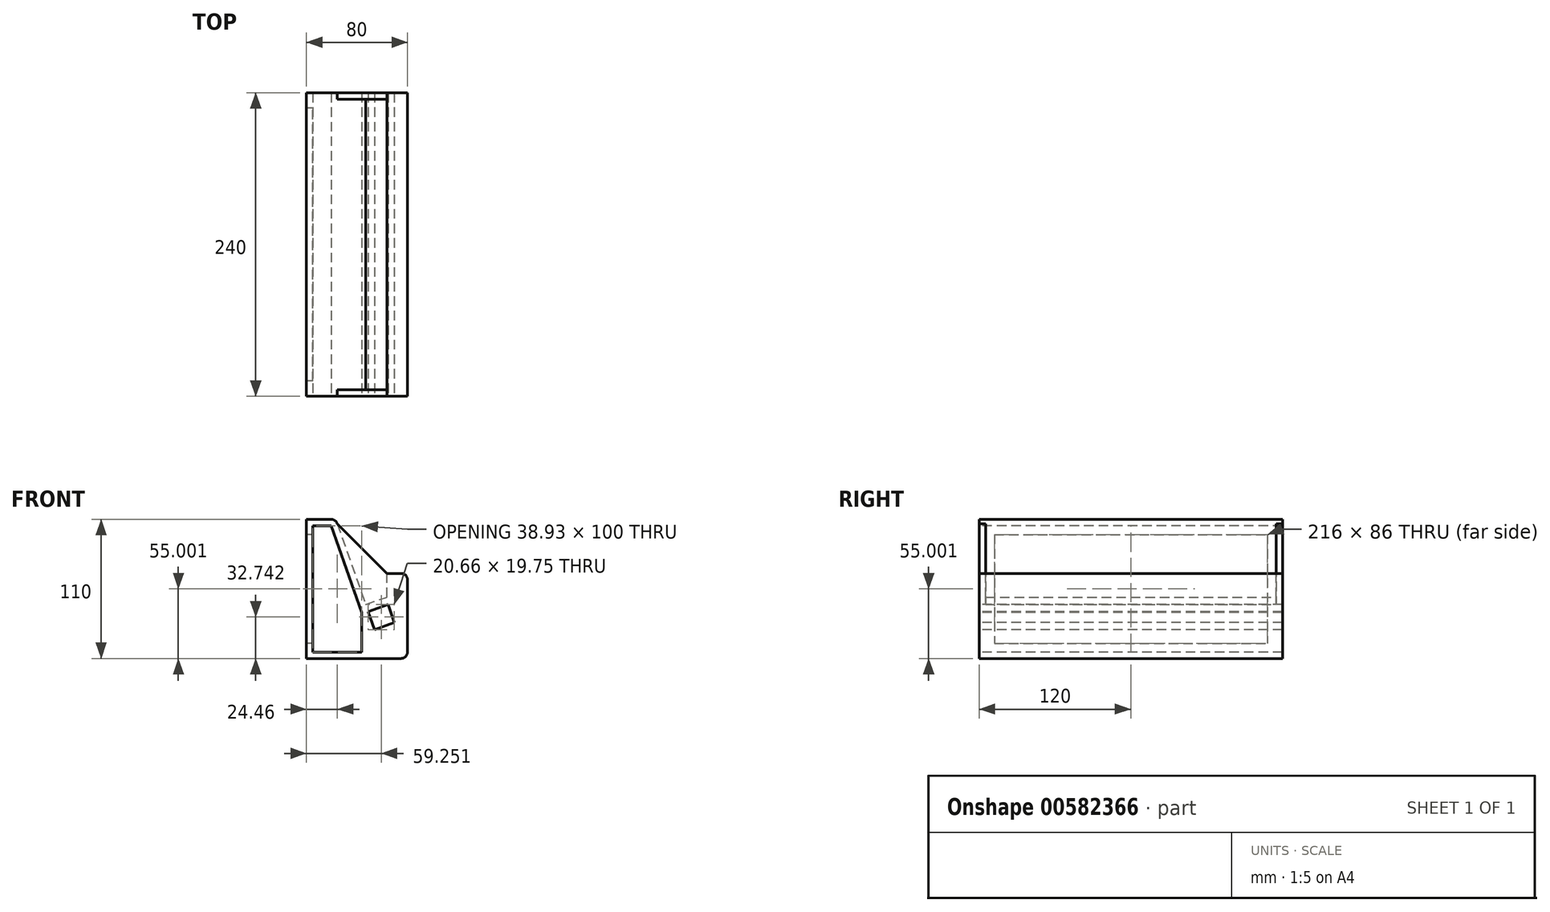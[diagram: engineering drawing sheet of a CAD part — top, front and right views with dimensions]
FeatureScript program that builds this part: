
annotation { "Feature Type Name" : "Feature", "Feature Type Description" : "" }
export const myFeature = defineFeature(function(context is Context, id is Id, definition is map)
    precondition{}
    {
        {
            var Q0;
            Q0=qCreatedBy(makeId("Front.planeOp"),FACE);
            var sketch = newSketch(context, id + "F0", { "sketchPlane" : qUnion([Q0])});
            skLineSegment(sketch, "E0.bottom", {"start": v(-111.66, 48.64) * mm, "end": v(-92, 48.64) * mm});
            skLineSegment(sketch, "E0.top", {"start": v(-111.66, -61.36) * mm, "end": v(-36.66, -61.36) * mm});
            skLineSegment(sketch, "E0.left", {"start": v(-111.66, 48.64) * mm, "end": v(-111.66, -61.36) * mm});
            skLineSegment(sketch, "E0.right", {"start": v(-31.66, 0.9) * mm, "end": v(-31.66, -56.36) * mm});
            skLineSegment(sketch, "E1", {"start": v(-87.28, 45.3) * mm, "end": v(-64.69, -18.74) * mm});
            skLineSegment(sketch, "E2", {"start": v(-64.69, -18.74) * mm, "end": v(-48.03, -12.87) * mm});
            skLineSegment(sketch, "E3", {"start": v(-48.03, -12.87) * mm, "end": v(-48.03, 5.9) * mm});
            skLineSegment(sketch, "E4", {"start": v(-48.03, 5.9) * mm, "end": v(-36.66, 5.9) * mm});
            skPoint(sketch, "E5.visualSharp", {"position": v(-88.46, 48.64) * mm});
            skArc(sketch, "E5.filletArc", {"start": v(-87.28, 45.3) * mm, "mid": v(-89.1, 47.72) * mm, "end": v(-92, 48.64) * mm});
            skPoint(sketch, "E6.visualSharp", {"position": v(-31.66, 5.9) * mm});
            skArc(sketch, "E6.filletArc", {"start": v(-31.66, 0.9) * mm, "mid": v(-33.13, 4.43) * mm, "end": v(-36.66, 5.9) * mm});
            skPoint(sketch, "E7.visualSharp", {"position": v(-31.66, -61.36) * mm});
            skArc(sketch, "E7.filletArc", {"start": v(-36.66, -61.36) * mm, "mid": v(-33.13, -59.9) * mm, "end": v(-31.66, -56.36) * mm});
            skLineSegment(sketch, "E8", {"start": v(-87.28, 45.3) * mm, "end": v(-48.03, 5.9) * mm});
            skSolve(sketch);
        }
        {
            var Q0;
            Q0=makeQuery(id+"F0.imprint","IMPRINT",FACE,{"disambiguationData":[TD([[makeQuery(id+"F0.imprint","IMPRINT",EDGE,{"derivedFrom":sQuery(id+"F0.wireOp",EDGE,"E0.bottom")}),-1.0]])]});
            extrude(context, id + "F1", {"entities" : qUnion([Q0]), "depth" : 240 * mm, "offsetDistance" : 25 * mm});
        }
        {
            var Q0;
            Q0=makeQuery(id+"F0.imprint","IMPRINT",FACE,{"disambiguationData":[TD([[makeQuery(id+"F0.imprint","IMPRINT",EDGE,{"derivedFrom":sQuery(id+"F0.wireOp",EDGE,"E1")}),1.0]])]});
            extrude(context, id + "F2", {"entities" : qUnion([Q0]), "operationType" : NewBodyOperationType.ADD, "depth" : 5 * mm, "offsetDistance" : 25 * mm});
        }
        {
            var Q0;
            Q0=makeQuery(id+"F1.opExtrude","CAP_FACE",FACE,{"disambiguationData":[OSD([sQuery(id+"F0.wireOp",EDGE,"E0.bottom"),sQuery(id+"F0.wireOp",EDGE,"E0.top"),sQuery(id+"F0.wireOp",EDGE,"E0.left"),sQuery(id+"F0.wireOp",EDGE,"E0.right"),sQuery(id+"F0.wireOp",EDGE,"E1"),sQuery(id+"F0.wireOp",EDGE,"E2"),sQuery(id+"F0.wireOp",EDGE,"E3"),sQuery(id+"F0.wireOp",EDGE,"E4"),sQuery(id+"F0.wireOp",EDGE,"E5.filletArc"),sQuery(id+"F0.wireOp",EDGE,"E6.filletArc"),sQuery(id+"F0.wireOp",EDGE,"E7.filletArc")])],"isStart":false});
            var sketch = newSketch(context, id + "F3", { "sketchPlane" : qUnion([Q0])});
            skLineSegment(sketch, "E9", {"start": v(-87.28, 45.3) * mm, "end": v(-48.03, 5.9) * mm});
            skLineSegment(sketch, "E10", {"start": v(-62.74, -24.26) * mm, "end": v(-47.1, -18.74) * mm});
            skLineSegment(sketch, "E11", {"start": v(-47.1, -18.74) * mm, "end": v(-42.08, -32.98) * mm});
            skLineSegment(sketch, "E12", {"start": v(-42.08, -32.98) * mm, "end": v(-57.7, -38.5) * mm});
            skLineSegment(sketch, "E13", {"start": v(-57.7, -38.5) * mm, "end": v(-62.74, -24.26) * mm});
            skSolve(sketch);
        }
        {
            var Q0;
            Q0=makeQuery(id+"F3.imprint","IMPRINT",FACE,{"disambiguationData":[TD([[makeQuery(id+"F3.imprint","IMPRINT",EDGE,{"derivedFrom":makeQuery(id+"F1.opExtrude","CAP_EDGE",EDGE,{"disambiguationData":[OSD([sQuery(id+"F0.wireOp",EDGE,"E0.bottom")])],"isStart":false})}),-1.0]])]});
            var sketch = newSketch(context, id + "F4", { "sketchPlane" : qUnion([Q0])});
            skLineSegment(sketch, "E14.0", {"start": v(-106.66, 43.64) * mm, "end": v(-106.66, -56.36) * mm});
            skLineSegment(sketch, "E14.1", {"start": v(-106.66, -56.36) * mm, "end": v(-67.74, -56.36) * mm});
            skLineSegment(sketch, "E14.2", {"start": v(-106.66, 43.64) * mm, "end": v(-92, 43.64) * mm});
            skLineSegment(sketch, "E14.4", {"start": v(-92, 43.64) * mm, "end": v(-67.74, -25.12) * mm});
            skLineSegment(sketch, "E15", {"start": v(-67.74, -25.12) * mm, "end": v(-67.74, -56.36) * mm});
            skSolve(sketch);
        }
        {
            var Q0;
            Q0=makeQuery(id+"F4.imprint","IMPRINT",FACE,{"disambiguationData":[TD([[makeQuery(id+"F4.imprint","IMPRINT",EDGE,{"derivedFrom":sQuery(id+"F4.wireOp",EDGE,"E14.0")}),1.0]])]});
            var Q1;
            Q1=sQuery(id+"F4.wireOp",EDGE,"E14.1");
            var Q2;
            Q2=sQuery(id+"F4.wireOp",EDGE,"E14.0");
            var Q3;
            Q3=sQuery(id+"F4.wireOp",EDGE,"E15");
            var Q4;
            Q4=sQuery(id+"F4.wireOp",EDGE,"E14.4");
            var Q5;
            Q5=sQuery(id+"F4.wireOp",EDGE,"E14.2");
            extrude(context, id + "F5", {"entities" : qUnion([Q0]), "operationType" : NewBodyOperationType.REMOVE, "surfaceEntities" : qUnion([Q1, Q2, Q3, Q4, Q5]), "oppositeDirection" : true, "depth" : 260 * mm, "offsetDistance" : 25 * mm});
        }
        {
            var Q0;
            Q0=makeQuery(id+"F3.imprint","IMPRINT",FACE,{"disambiguationData":[TD([[makeQuery(id+"F3.imprint","IMPRINT",EDGE,{"derivedFrom":sQuery(id+"F3.wireOp",EDGE,"E10")}),-1.0]])]});
            extrude(context, id + "F6", {"entities" : qUnion([Q0]), "operationType" : NewBodyOperationType.REMOVE, "oppositeDirection" : true, "depth" : 252 * mm, "offsetDistance" : 25 * mm});
        }
        {
            var Q0;
            Q0=makeQuery(id+"F3.imprint","IMPRINT",FACE,{"disambiguationData":[TD([[makeQuery(id+"F3.imprint","IMPRINT",EDGE,{"derivedFrom":sQuery(id+"F3.wireOp",EDGE,"E9")}),-1.0]])]});
            var sketch = newSketch(context, id + "F7", { "sketchPlane" : qUnion([Q0])});
            skSolve(sketch);
        }
        {
            var Q0;
            Q0 = qSketchRegion(id + "F7", true);
            var Q1;
            Q1=makeQuery(id+"F7.imprint","IMPRINT",FACE,{"disambiguationData":[TD([[makeQuery(id+"F7.imprint","IMPRINT",EDGE,{"derivedFrom":makeQuery(id+"F3.imprint","IMPRINT",EDGE,{"derivedFrom":sQuery(id+"F3.wireOp",EDGE,"E9")})}),-1.0]])]});
            extrude(context, id + "F8", {"entities" : qUnion([Q0, Q1]), "operationType" : NewBodyOperationType.ADD, "oppositeDirection" : true, "depth" : 5 * mm, "offsetDistance" : 25 * mm});
        }
        {
            var Q0;
            Q0=makeQuery(id+"F1.opExtrude","SWEPT_FACE",FACE,{"disambiguationData":[OSD([sQuery(id+"F0.wireOp",EDGE,"E0.left")])]});
            var sketch = newSketch(context, id + "F9", { "sketchPlane" : qUnion([Q0])});
            skLineSegment(sketch, "E16.0", {"start": v(228, 36.64) * mm, "end": v(228, -49.36) * mm});
            skLineSegment(sketch, "E16.1", {"start": v(12, 36.64) * mm, "end": v(12, 5.9) * mm});
            skLineSegment(sketch, "E16.2", {"start": v(12, 0.9) * mm, "end": v(12, 5.9) * mm});
            skLineSegment(sketch, "E16.3", {"start": v(228, 36.64) * mm, "end": v(12, 36.64) * mm});
            skLineSegment(sketch, "E16.4", {"start": v(12, 0.9) * mm, "end": v(12, -49.36) * mm});
            skLineSegment(sketch, "E16.5", {"start": v(228, -49.36) * mm, "end": v(12, -49.36) * mm});
            skSolve(sketch);
        }
        {
            var Q0;
            Q0=makeQuery(id+"F9.imprint","IMPRINT",FACE,{"disambiguationData":[TD([[makeQuery(id+"F9.imprint","IMPRINT",EDGE,{"derivedFrom":sQuery(id+"F9.wireOp",EDGE,"E16.0")}),-1.0]])]});
            extrude(context, id + "F10", {"entities" : qUnion([Q0]), "operationType" : NewBodyOperationType.REMOVE, "oppositeDirection" : true, "depth" : 5 * mm, "offsetDistance" : 25 * mm});
        }
    });
